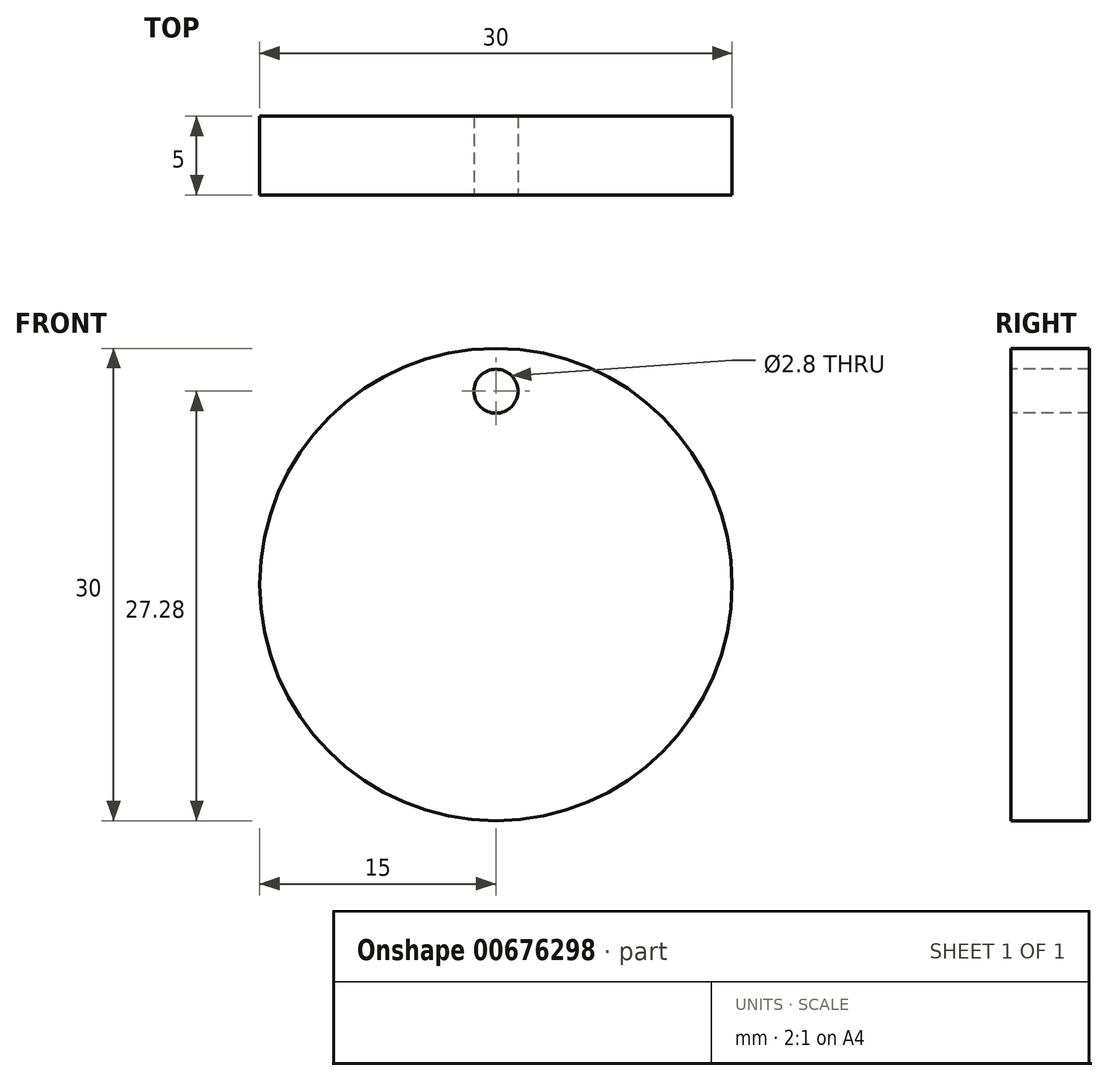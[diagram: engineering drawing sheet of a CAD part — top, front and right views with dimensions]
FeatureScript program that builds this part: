
annotation { "Feature Type Name" : "Feature", "Feature Type Description" : "" }
export const myFeature = defineFeature(function(context is Context, id is Id, definition is map)
    precondition{}
    {
        {
            var Q0;
            Q0=qCreatedBy(makeId("Front.planeOp"),FACE);
            var sketch = newSketch(context, id + "F0", { "sketchPlane" : qUnion([Q0])});
            skCircle(sketch, "E0", {"center": v(0, 0) * mm, "radius": 15 * mm});
            skSolve(sketch);
        }
        {
            var Q0;
            Q0=makeQuery(id+"F0.imprint","IMPRINT",FACE,{"disambiguationData":[TD([[makeQuery(id+"F0.imprint","IMPRINT",EDGE,{"derivedFrom":sQuery(id+"F0.wireOp",EDGE,"E0")}),1.0]])]});
            extrude(context, id + "F1", {"entities" : qUnion([Q0]), "depth" : 5 * mm, "offsetDistance" : 25 * mm});
        }
        {
            var Q0;
            Q0=makeQuery(id+"F1.opExtrude","CAP_FACE",FACE,{"disambiguationData":[OSD([sQuery(id+"F0.wireOp",EDGE,"E0")])],"isStart":false});
            var sketch = newSketch(context, id + "F2", { "sketchPlane" : qUnion([Q0])});
            skCircle(sketch, "E1", {"center": v(0, 12.28) * mm, "radius": 1.4 * mm});
            skSolve(sketch);
        }
        {
            var Q0;
            Q0=makeQuery(id+"F2.imprint","IMPRINT",FACE,{"disambiguationData":[TD([[makeQuery(id+"F2.imprint","IMPRINT",EDGE,{"derivedFrom":sQuery(id+"F2.wireOp",EDGE,"ZBxxBG9J-vWCq-D6Lm-P3dy-BCEz2WmIfDc8")}),1.0]])]});
            var Q1;
            Q1=makeQuery(id+"F2.imprint","IMPRINT",FACE,{"disambiguationData":[TD([[makeQuery(id+"F2.imprint","IMPRINT",EDGE,{"derivedFrom":sQuery(id+"F2.wireOp",EDGE,"E1")}),1.0]])]});
            var Q2;
            Q2=sQuery(id+"F2.wireOp",EDGE,"ZBxxBG9J-vWCq-D6Lm-P3dy-BCEz2WmIfDc8");
            extrude(context, id + "F3", {"entities" : qUnion([Q0, Q1]), "operationType" : NewBodyOperationType.REMOVE, "surfaceEntities" : qUnion([Q2]), "oppositeDirection" : true, "depth" : 5 * mm, "offsetDistance" : 25 * mm});
        }
    });
